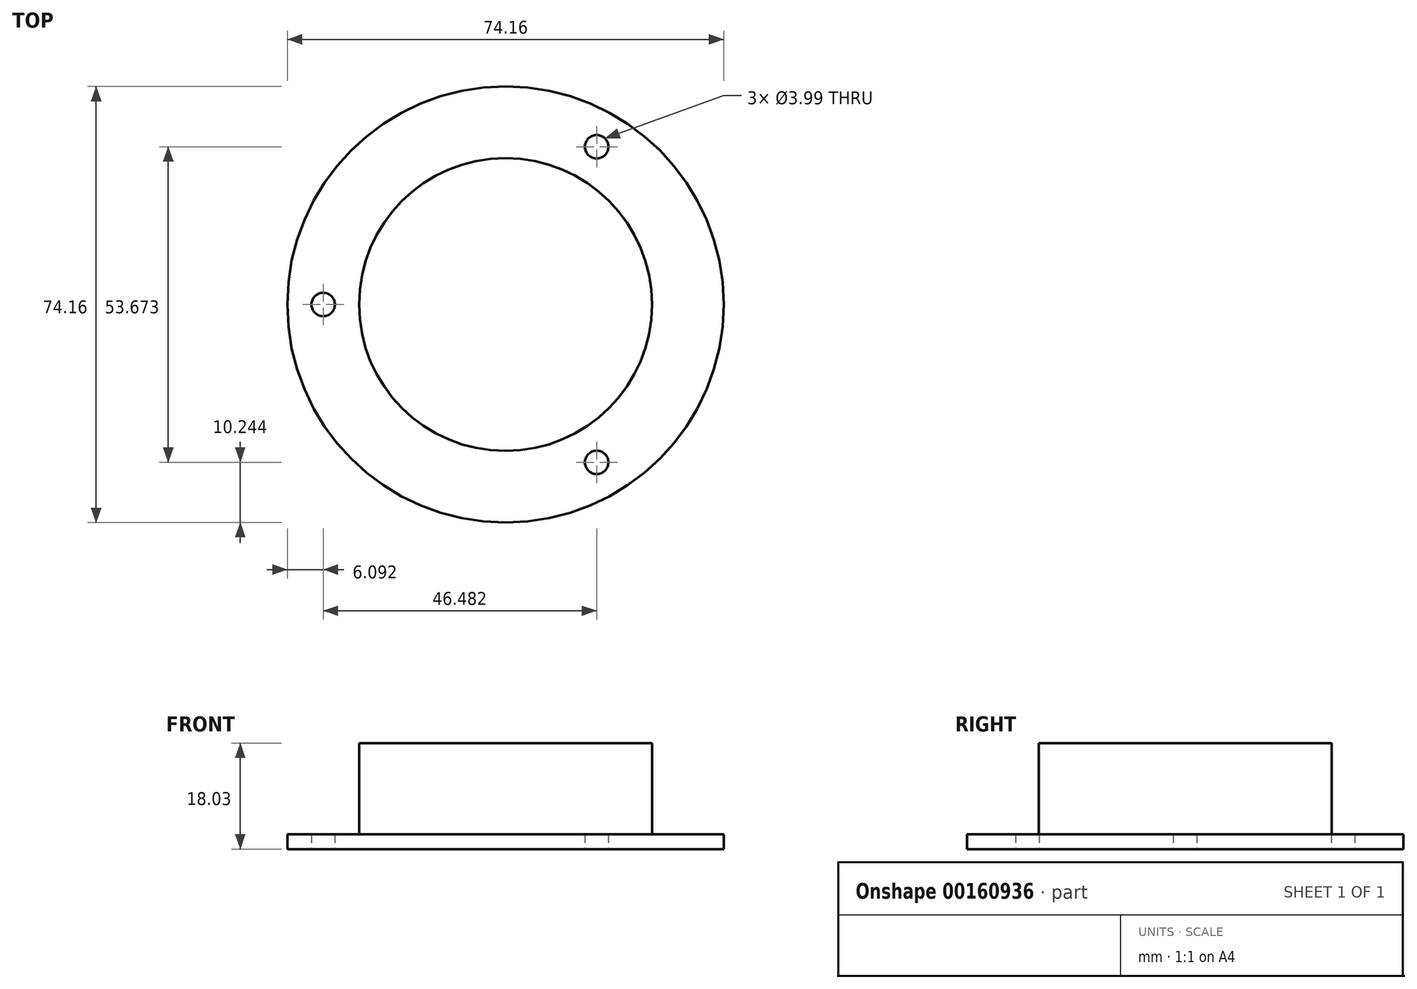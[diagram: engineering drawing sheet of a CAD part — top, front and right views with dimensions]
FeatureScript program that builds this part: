
annotation { "Feature Type Name" : "Feature", "Feature Type Description" : "" }
export const myFeature = defineFeature(function(context is Context, id is Id, definition is map)
    precondition{}
    {
        {
            var Q0;
            Q0=qCreatedBy(makeId("Top.planeOp"),FACE);
            var sketch = newSketch(context, id + "F0", { "sketchPlane" : qUnion([Q0])});
            skCircle(sketch, "E0", {"center": v(0, 0) * mm, "radius": 37.08 * mm});
            skCircle(sketch, "E1", {"center": v(0, 0) * mm, "radius": 24.9 * mm});
            skLineSegment(sketch, "E2", {"start": v(0, 0) * mm, "end": v(25.18, 43.6) * mm, "construction": true});
            skLineSegment(sketch, "E3", {"start": v(-24.9, 0) * mm, "end": v(-37.08, 0) * mm});
            skPoint(sketch, "E4", {"position": v(-30.99, 0) * mm});
            skCircle(sketch, "E5", {"center": v(-30.99, 0) * mm, "radius": 2 * mm});
            skCircle(sketch, "E6.MirrorC", {"center": v(15.5, -26.84) * mm, "radius": 2 * mm});
            skLineSegment(sketch, "E7", {"start": v(0, 0) * mm, "end": v(-24.32, 42.12) * mm, "construction": true});
            skCircle(sketch, "E8.MirrorC", {"center": v(15.5, 26.84) * mm, "radius": 2 * mm});
            skSolve(sketch);
        }
        {
            var Q0;
            Q0=makeQuery(id+"F0.imprint","IMPRINT",FACE,{"disambiguationData":[TD([[makeQuery(id+"F0.imprint","IMPRINT",EDGE,{"derivedFrom":sQuery(id+"F0.wireOp",EDGE,"E1")}),1.0]])]});
            extrude(context, id + "F1", {"entities" : qUnion([Q0]), "depth" : 18.03 * mm});
        }
        {
            var Q0;
            Q0=makeQuery(id+"F0.imprint","IMPRINT",FACE,{"disambiguationData":[TD([[makeQuery(id+"F0.imprint","IMPRINT",EDGE,{"derivedFrom":sQuery(id+"F0.wireOp",EDGE,"E0")}),1.0]])]});
            var Q1;
            Q1=makeQuery(id+"F0.imprint","IMPRINT",FACE,{"disambiguationData":[TD([[makeQuery(id+"F0.imprint","IMPRINT",EDGE,{"derivedFrom":sQuery(id+"F0.wireOp",EDGE,"f8d507d4-32da-4c17-811f-1a31e90968720.MirrorC")}),1.0]])]});
            extrude(context, id + "F2", {"entities" : qUnion([Q0, Q1]), "operationType" : NewBodyOperationType.ADD, "depth" : 2.54 * mm});
        }
    });
